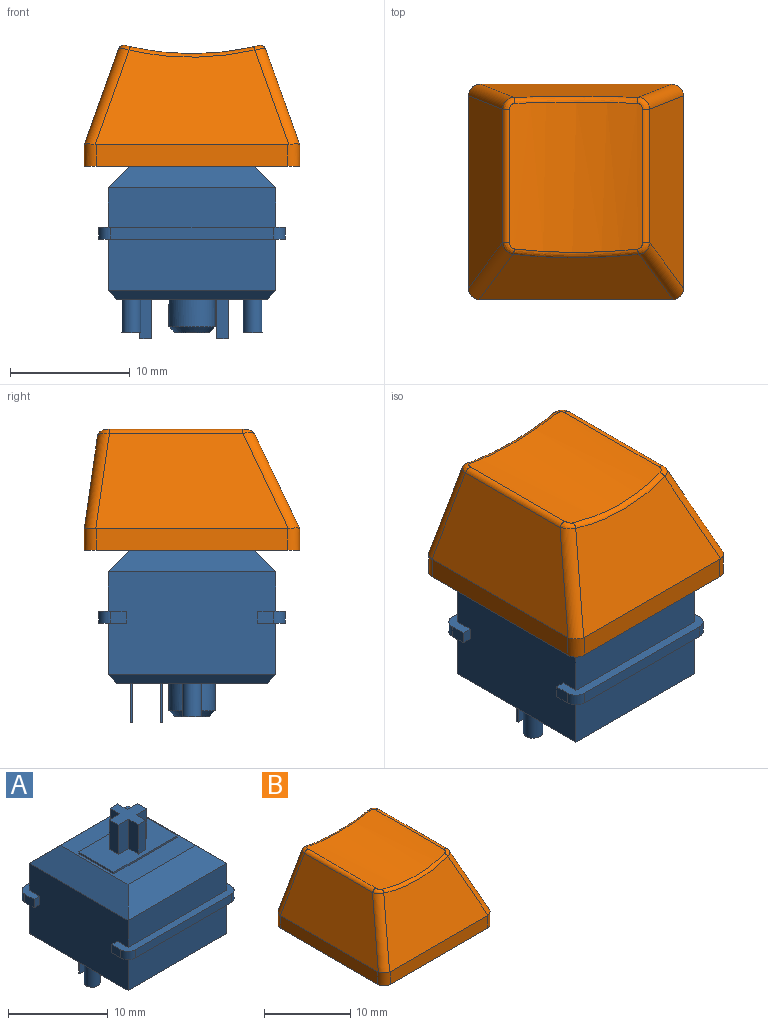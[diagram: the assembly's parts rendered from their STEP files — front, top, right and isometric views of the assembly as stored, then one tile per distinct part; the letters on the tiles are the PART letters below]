
ASSEMBLY  parts=2 mates=1
PART A: 69 faces, bbox 15.6x15.6x18.6 mm
  f0: plane 15.6x2.3mm, normal (0,0,-1), area 14.4mm2, adj f2,f3,f28,f30,f35,f60,f62,f63
  f1: plane 15.6x2.3mm, normal (0,0,-1), area 14.4mm2, adj f28,f30,f33,f34,f36,f59,f61,f64
  f2: plane 1.3x1mm, normal (1,0,0), area 1.3mm2, adj f0,f32,f62,f66
  f3: plane 1.3x1mm, normal (-1,0,0), area 1.3mm2, adj f0,f32,f63,f68
  f4: plane 15.6x2.3mm, normal (0,0,1), area 14.4mm2, adj f28,f30,f31,f33,f34,f36,f61,f64
  f5: plane 14x2.2mm, normal (-0.71,0,0.71), area 36.7mm2, adj f6,f7,f26,f30
  f6: plane 14x2.2mm, normal (0,-0.71,0.71), area 36.7mm2, adj f5,f7,f27,f31
  f7: plane 9.6x9.6mm, normal (0,0,1), area 47.2mm2, adj f5,f6,f8,f9,f10,f11,f26,f27
  f8: plane 5x0.2mm, normal (1,0,0), area 1mm2, adj f7,f9,f11,f12
  f9: plane 9x0.2mm, normal (0,1,0), area 1.8mm2, adj f7,f8,f10,f12
  f10: plane 5x0.2mm, normal (-1,0,0), area 1mm2, adj f7,f9,f11,f12
  f11: plane 9x0.2mm, normal (0,-1,0), area 1.8mm2, adj f7,f8,f10,f12
  f12: plane 9x5mm, normal (0,0,1), area 36.9mm2, adj f8,f9,f10,f11,f13,f14,f15,f16
  f13: plane 3.6x1.35mm, normal (1,0,0), area 4.9mm2, adj f12,f14,f24,f25
  f14: plane 3.6x1.08mm, normal (0,1,0), area 3.9mm2, adj f12,f13,f15,f25
  f15: plane 3.6x1.35mm, normal (-1,0,0), area 4.9mm2, adj f12,f14,f16,f25
  f16: plane 3.6x1.46mm, normal (0,1,0), area 5.3mm2, adj f12,f15,f17,f25
  f17: plane 3.6x1.3mm, normal (-1,0,0), area 4.7mm2, adj f12,f16,f18,f25
  f18: plane 3.6x1.46mm, normal (0,-1,0), area 5.3mm2, adj f12,f17,f19,f25
  f19: plane 3.6x1.35mm, normal (-1,0,0), area 4.9mm2, adj f12,f18,f20,f25
  f20: plane 3.6x1.08mm, normal (0,-1,0), area 3.9mm2, adj f12,f19,f21,f25
  f21: plane 3.6x1.35mm, normal (1,0,0), area 4.9mm2, adj f12,f20,f22,f25
  f22: plane 3.6x1.46mm, normal (0,-1,0), area 5.3mm2, adj f12,f21,f23,f25
  f23: plane 3.6x1.3mm, normal (1,0,0), area 4.7mm2, adj f12,f22,f24,f25
  f24: plane 3.6x1.46mm, normal (0,1,0), area 5.3mm2, adj f12,f13,f23,f25
  f25: plane 4x4mm, normal (0,0,1), area 8.1mm2, adj f13,f14,f15,f16,f17,f18,f19,f20
  f26: plane 14x2.2mm, normal (0,0.71,0.71), area 36.7mm2, adj f5,f7,f27,f29
  f27: plane 14x2.2mm, normal (0.71,0,0.71), area 36.7mm2, adj f6,f7,f26,f28
  f28: plane 14x8.6mm, normal (1,0,0), area 117.4mm2, adj f0,f1,f4,f27,f29,f31,f32,f55
  f29: plane 14x3.3mm, normal (0,1,0), area 46.2mm2, adj f26,f28,f30,f32
  f30: plane 14x8.6mm, normal (-1,0,0), area 117.4mm2, adj f0,f1,f4,f5,f29,f31,f32,f57
  f31: plane 14x3.3mm, normal (0,-1,0), area 46.2mm2, adj f4,f6,f28,f30
  f32: plane 15.6x2.3mm, normal (0,0,1), area 14.4mm2, adj f2,f3,f28,f29,f30,f35,f62,f63
  f33: plane 13.6x1mm, normal (0,-1,0), area 13.6mm2, adj f1,f4,f61,f64
  f34: plane 1.3x1mm, normal (1,0,0), area 1.3mm2, adj f1,f4,f61,f65
  f35: plane 13.6x1mm, normal (0,1,0), area 13.6mm2, adj f0,f32,f62,f63
  f36: plane 1.3x1mm, normal (-1,0,0), area 1.3mm2, adj f1,f4,f64,f67
  f37: plane 2.85x2.85mm, normal (0,0,-1), area 6.4mm2, adj f38
  f38: cone r=1.43mm half-angle=45deg, axis (0,0,1), area 7.4mm2, adj f37,f43
  f39: plane 1x0.2mm, normal (0,0,-1), area 0.2mm2, adj f44,f45,f46,f47
  f40: plane 1x0.2mm, normal (0,0,-1), area 0.2mm2, adj f48,f49,f50,f51
  f41: plane 1.6x1.6mm, normal (0,0,-1), area 2mm2, adj f52
  f42: plane 1.6x1.6mm, normal (0,0,-1), area 2mm2, adj f53
  f43: cylinder r=1.93mm len=3.85mm, axis (0,0,1), area 27.8mm2, adj f38,f54
  f44: plane 3.3x0.2mm, normal (-1,0,0), area 0.7mm2, adj f39,f45,f47,f54
  f45: plane 3.3x1mm, normal (0,1,0), area 3.3mm2, adj f39,f44,f46,f54
  f46: plane 3.3x0.2mm, normal (1,0,0), area 0.7mm2, adj f39,f45,f47,f54
  f47: plane 3.3x1mm, normal (0,-1,0), area 3.3mm2, adj f39,f44,f46,f54
  f48: plane 3.3x0.2mm, normal (-1,0,0), area 0.7mm2, adj f40,f49,f51,f54
  f49: plane 3.3x1mm, normal (0,1,0), area 3.3mm2, adj f40,f48,f50,f54
  f50: plane 3.3x0.2mm, normal (1,0,0), area 0.7mm2, adj f40,f49,f51,f54
  f51: plane 3.3x1mm, normal (0,-1,0), area 3.3mm2, adj f40,f48,f50,f54
  f52: cylinder r=0.8mm len=2.8mm, axis (0,0,1), area 14.1mm2, adj f41,f54
  f53: cylinder r=0.8mm len=2.8mm, axis (0,0,1), area 14.1mm2, adj f42,f54
  f54: plane 12.6x12.6mm, normal (0,0,-1), area 142.7mm2, adj f43,f44,f45,f46,f47,f48,f49,f50
  f55: plane 14x0.7mm, normal (0.71,0,-0.71), area 13.2mm2, adj f28,f54,f56,f58
  f56: plane 14x0.7mm, normal (0,0.71,-0.71), area 13.2mm2, adj f54,f55,f57,f60
  f57: plane 14x0.7mm, normal (-0.71,0,-0.71), area 13.2mm2, adj f30,f54,f56,f58
  f58: plane 14x0.7mm, normal (0,-0.71,-0.71), area 13.2mm2, adj f54,f55,f57,f59
  f59: plane 14x4.3mm, normal (0,-1,0), area 60.2mm2, adj f1,f28,f30,f58
  f60: plane 14x4.3mm, normal (0,1,0), area 60.2mm2, adj f0,f28,f30,f56
  f61: cylinder r=1mm len=1mm, axis (0,0,-1), area 1.6mm2, adj f1,f4,f33,f34
  f62: cylinder r=1mm len=1mm, axis (0,0,1), area 1.6mm2, adj f0,f2,f32,f35
  f63: cylinder r=1mm len=1mm, axis (0,0,-1), area 1.6mm2, adj f0,f3,f32,f35
  f64: cylinder r=1mm len=1mm, axis (0,0,1), area 1.6mm2, adj f1,f4,f33,f36
  f65: plane 1x0.8mm, normal (0,1,0), area 0.8mm2, adj f1,f4,f28,f34
  f66: plane 1x0.8mm, normal (0,-1,0), area 0.8mm2, adj f0,f2,f28,f32
  f67: plane 1x0.8mm, normal (0,1,0), area 0.8mm2, adj f1,f4,f30,f36
  f68: plane 1x0.8mm, normal (0,-1,0), area 0.8mm2, adj f0,f3,f30,f32
PART B: 50 faces, bbox 18.1x18x10.2 mm
  f0: plane 18x18mm, normal (0,0,-1), area 67.1mm2, adj f1,f2,f3,f4,f10,f12,f14,f16
  f1: plane 16x1.8mm, normal (1,0,0), area 28.8mm2, adj f0,f8,f10,f16
  f2: plane 16x1.8mm, normal (0,1,0), area 28.8mm2, adj f0,f5,f14,f15,f16,f17
  f3: plane 16x1.8mm, normal (-1,0,0), area 28.8mm2, adj f0,f6,f12,f14
  f4: plane 16x1.8mm, normal (0,-1,0), area 28.8mm2, adj f0,f7,f10,f12
  f5: plane 15.98x7.76mm, normal (0,0.99,0.14), area 99.4mm2, adj f2,f15,f17,f20
  f6: plane 16.09x7.97mm, normal (-0.94,0,0.34), area 115.3mm2, adj f3,f12,f13,f14,f15,f19
  f7: plane 16.18x7.92mm, normal (0,-0.9,0.43), area 112.4mm2, adj f4,f10,f11,f12,f13,f23
  f8: plane 16.09x7.97mm, normal (0.94,0,0.34), area 115.3mm2, adj f1,f10,f11,f16,f17,f24
  f9: cylinder r=22.9mm len=12.55mm, axis (0,-1,0), area 139.2mm2, adj f18,f19,f20,f21,f22,f23,f24,f25
  f10: cylinder r=1mm len=1.87mm, axis (0,0,-1), area 2.9mm2, adj f0,f1,f4,f7,f8,f11
  f11: cylinder r=1mm len=8.25mm, axis (0.31,-0.41,-0.86), area 13.2mm2, adj f7,f8,f10,f25
  f12: cylinder r=1mm len=1.87mm, axis (0,0,1), area 2.9mm2, adj f0,f3,f4,f6,f7,f13
  f13: cylinder r=1mm len=8.25mm, axis (0.31,0.41,0.86), area 13.2mm2, adj f6,f7,f12,f21
  f14: cylinder r=1mm len=1.83mm, axis (0,0,-1), area 2.9mm2, adj f0,f2,f3,f6,f15
  f15: cylinder r=1mm len=8.19mm, axis (-0.33,0.13,-0.93), area 12.9mm2, adj f2,f5,f6,f14,f18
  f16: cylinder r=1mm len=1.83mm, axis (0,0,1), area 2.9mm2, adj f0,f1,f2,f8,f17
  f17: cylinder r=1mm len=8.19mm, axis (-0.33,-0.13,0.93), area 12.9mm2, adj f2,f5,f8,f16,f22
  f18: bspline ~1.24x1.22mm, area 0.9mm2, adj f9,f15,f19,f20
  f19: cylinder r=0.5mm len=11.16mm, axis (0,-1,0), area 8.2mm2, adj f6,f9,f18,f21
  f20: bspline ~10.43x1.01mm, area 7.4mm2, adj f5,f9,f18,f22
  f21: bspline ~1.23x1.15mm, area 0.7mm2, adj f9,f13,f19,f23
  f22: bspline ~1.24x1.22mm, area 0.9mm2, adj f9,f17,f20,f24
  f23: bspline ~10.53x0.87mm, area 5.9mm2, adj f7,f9,f21,f25
  f24: cylinder r=0.5mm len=11.16mm, axis (0,-1,0), area 8.2mm2, adj f8,f9,f22,f25
  f25: bspline ~1.23x1.15mm, area 0.7mm2, adj f9,f11,f23,f24
  f26: plane 16x1.63mm, normal (-1,0,0), area 26mm2, adj f0,f27,f29,f32,f33
  f27: plane 16x1.73mm, normal (0,-1,0), area 27.7mm2, adj f0,f26,f28,f30,f31,f33
  f28: plane 16x1.63mm, normal (1,0,0), area 26mm2, adj f0,f27,f29,f31,f32
  f29: plane 16x1.57mm, normal (0,1,0), area 25.2mm2, adj f0,f26,f28,f32
  f30: plane 15.93x7.28mm, normal (0,-0.99,-0.14), area 93.6mm2, adj f27,f31,f33,f34
  f31: plane 15.98x7.38mm, normal (0.94,0,-0.34), area 107.4mm2, adj f27,f28,f30,f32,f34
  f32: plane 16x7.44mm, normal (0,0.9,-0.43), area 105.4mm2, adj f26,f28,f29,f31,f33,f34
  f33: plane 15.98x7.38mm, normal (-0.94,0,-0.34), area 107.4mm2, adj f26,f27,f30,f32,f34
  f34: cylinder r=23.9mm len=11.8mm, axis (0,-1,0), area 102.5mm2, adj f30,f31,f32,f33,f46
  f35: plane 7.81x1.5mm, normal (-1,0,0), area 11.7mm2, adj f36,f44,f45,f49
  f36: plane 7.9x1.5mm, normal (0,-1,0), area 11.8mm2, adj f35,f37,f45,f49
  f37: plane 7.9x1.3mm, normal (-1,0,0), area 10.3mm2, adj f36,f38,f45,f49
  f38: plane 7.9x1.5mm, normal (0,1,0), area 11.8mm2, adj f37,f39,f45,f49
  f39: plane 7.81x1.5mm, normal (-1,0,0), area 11.7mm2, adj f38,f40,f45,f49
  f40: plane 7.81x1.3mm, normal (0,1,0), area 10.1mm2, adj f39,f41,f45,f49
  f41: plane 7.81x1.5mm, normal (1,0,0), area 11.7mm2, adj f40,f42,f45,f49
  f42: plane 7.9x1.5mm, normal (0,1,0), area 11.8mm2, adj f41,f43,f45,f49
  f43: plane 7.9x1.3mm, normal (1,0,0), area 10.3mm2, adj f42,f45,f47,f49
  f44: plane 7.81x1.3mm, normal (0,-1,0), area 10.1mm2, adj f35,f45,f48,f49
  f45: plane 5.5x5.5mm, normal (0,0,-1), area 14.3mm2, adj f35,f36,f37,f38,f39,f40,f41,f42
  f46: cylinder r=2.75mm len=7.96mm, axis (0,0,-1), area 136.1mm2, adj f34,f45
  f47: plane 7.9x1.5mm, normal (0,-1,0), area 11.8mm2, adj f43,f45,f48,f49
  f48: plane 7.81x1.5mm, normal (1,0,0), area 11.7mm2, adj f44,f45,f47,f49
  f49: cylinder r=23.9mm len=4.3mm, axis (0,-1,0), area 9.5mm2, adj f35,f36,f37,f38,f39,f40,f41,f42
PLACE A at identity fixed
PLACE B t=(0,0,11.1)mm
MATE fastened B.f46 <-> A.f38  axis (0,0,-1) through (0,0,11.7)mm
